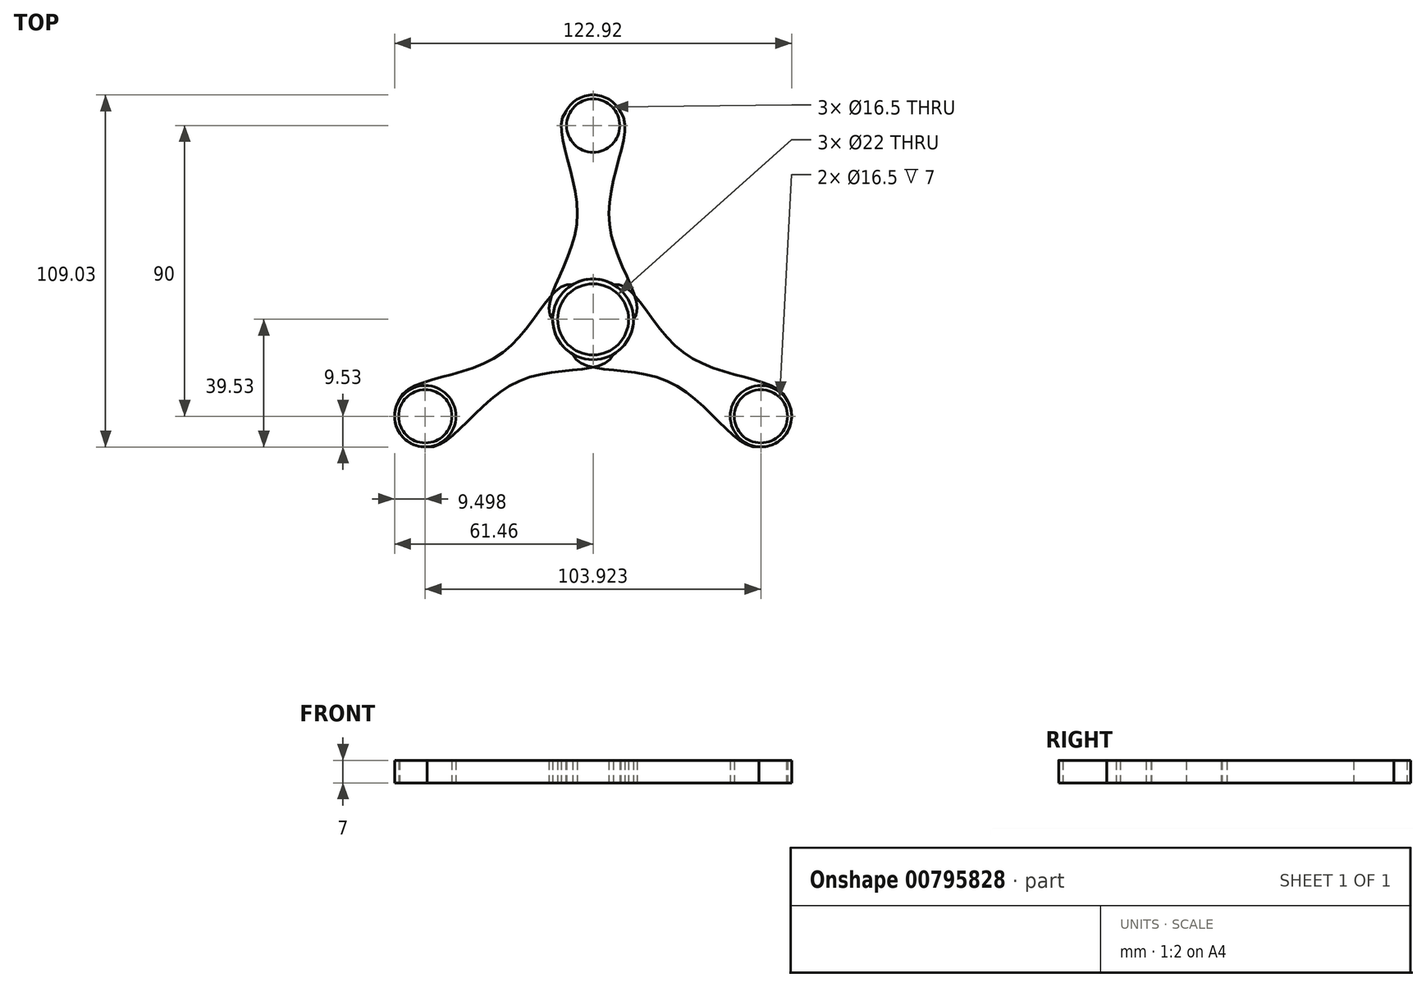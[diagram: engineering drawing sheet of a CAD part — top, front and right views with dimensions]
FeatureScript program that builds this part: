
annotation { "Feature Type Name" : "Feature", "Feature Type Description" : "" }
export const myFeature = defineFeature(function(context is Context, id is Id, definition is map)
    precondition{}
    {
        {
            var Q0;
            Q0=qCreatedBy(makeId("Top.planeOp"),FACE);
            var sketch = newSketch(context, id + "F0", { "sketchPlane" : qUnion([Q0])});
            skCircle(sketch, "E0", {"center": v(0, 0) * mm, "radius": 11 * mm});
            skLineSegment(sketch, "E1", {"start": v(0, 0) * mm, "end": v(0, 60) * mm});
            skLineSegment(sketch, "E2.1.0", {"start": v(0, 0) * mm, "end": v(-51.96, -30) * mm});
            skLineSegment(sketch, "E2.2.0", {"start": v(0, 0) * mm, "end": v(51.96, -30) * mm});
            skCircle(sketch, "E3", {"center": v(0, 60) * mm, "radius": 8.25 * mm});
            skCircle(sketch, "E4.1.0", {"center": v(-51.96, -30) * mm, "radius": 8.25 * mm});
            skCircle(sketch, "E4.2.0", {"center": v(51.96, -30) * mm, "radius": 8.25 * mm});
            skCircle(sketch, "E5", {"center": v(0, 60) * mm, "radius": 9.5 * mm});
            skCircle(sketch, "E6", {"center": v(0, 0) * mm, "radius": 12.5 * mm});
            skCircle(sketch, "E7.1.0", {"center": v(-51.96, -30) * mm, "radius": 9.5 * mm});
            skCircle(sketch, "E7.2.0", {"center": v(51.96, -30) * mm, "radius": 9.5 * mm});
            skPoint(sketch, "E8.1.internal.snap0", {"position": v(0, 30) * mm});
            skPoint(sketch, "E8.4.internal.snap0", {"position": v(0, 30) * mm});
            skFitSpline(sketch, "E8", {"points": [v(-8.52, 64.2) * mm, v(-5, 30) * mm, v(-12.5, 0) * mm, v(12.5, 0) * mm, v(5, 30) * mm, v(8.52, 64.2) * mm, v(-8.52, 64.2) * mm]});
            skSolve(sketch);
        }
        {
            var Q0;
            {var subQ0=sQuery(id+"F0.wireOp",EDGE,"E6");var subQ1=sQuery(id+"F0.wireOp",EDGE,"E1");var subQ2=makeQuery(id+"F0.imprint","INTERSECT",VERTEX,{"derivedFrom":[subQ1,subQ0]});Q0=makeQuery(id+"F0.imprint","IMPRINT",FACE,{"disambiguationData":[TD([[makeQuery(id+"F0.imprint","IMPRINT",EDGE,{"disambiguationData":[TD([[subQ2,-1.0]])],"derivedFrom":subQ1}),1.0]])]});}
            var Q1;
            {var subQ0=sQuery(id+"F0.wireOp",EDGE,"E6");var subQ1=sQuery(id+"F0.wireOp",EDGE,"E1");var subQ2=makeQuery(id+"F0.imprint","INTERSECT",VERTEX,{"derivedFrom":[subQ1,subQ0]});Q1=makeQuery(id+"F0.imprint","IMPRINT",FACE,{"disambiguationData":[TD([[makeQuery(id+"F0.imprint","IMPRINT",EDGE,{"disambiguationData":[TD([[subQ2,-1.0]])],"derivedFrom":subQ1}),-1.0]])]});}
            var Q2;
            {var subQ0=sQuery(id+"F0.wireOp",EDGE,"E8");var subQ1=sQuery(id+"F0.wireOp",EDGE,"E3");var subQ2=makeQuery(id+"F0.imprint","INTERSECT",VERTEX,{"disambiguationData":[OD(0.0)],"derivedFrom":[subQ1,subQ0]});Q2=makeQuery(id+"F0.imprint","IMPRINT",FACE,{"disambiguationData":[TD([[makeQuery(id+"F0.imprint","IMPRINT",EDGE,{"disambiguationData":[TD([[subQ2,1.0]])],"derivedFrom":subQ1}),-1.0]])]});}
            var Q3;
            {var subQ0=sQuery(id+"F0.wireOp",EDGE,"E3");var subQ1=sQuery(id+"F0.wireOp",EDGE,"E1");var subQ2=makeQuery(id+"F0.imprint","INTERSECT",VERTEX,{"derivedFrom":[subQ1,subQ0]});Q3=makeQuery(id+"F0.imprint","IMPRINT",FACE,{"disambiguationData":[TD([[makeQuery(id+"F0.imprint","IMPRINT",EDGE,{"disambiguationData":[TD([[subQ2,1.0]])],"derivedFrom":subQ1}),1.0]])]});}
            var Q4;
            {var subQ0=sQuery(id+"F0.wireOp",EDGE,"E3");var subQ1=sQuery(id+"F0.wireOp",EDGE,"E1");var subQ2=makeQuery(id+"F0.imprint","INTERSECT",VERTEX,{"derivedFrom":[subQ1,subQ0]});Q4=makeQuery(id+"F0.imprint","IMPRINT",FACE,{"disambiguationData":[TD([[makeQuery(id+"F0.imprint","IMPRINT",EDGE,{"disambiguationData":[TD([[subQ2,1.0]])],"derivedFrom":subQ1}),-1.0]])]});}
            var Q5;
            {var subQ0=sQuery(id+"F0.wireOp",EDGE,"E8");var subQ1=sQuery(id+"F0.wireOp",EDGE,"E0");var subQ2=makeQuery(id+"F0.imprint","INTERSECT",VERTEX,{"disambiguationData":[OD(0.0)],"derivedFrom":[subQ1,subQ0]});Q5=makeQuery(id+"F0.imprint","IMPRINT",FACE,{"disambiguationData":[TD([[makeQuery(id+"F0.imprint","IMPRINT",EDGE,{"disambiguationData":[TD([[subQ2,1.0]])],"derivedFrom":subQ1}),-1.0]])]});}
            var Q6;
            {var subQ0=sQuery(id+"F0.wireOp",EDGE,"E1");var subQ1=sQuery(id+"F0.wireOp",EDGE,"E0");var subQ2=makeQuery(id+"F0.imprint","INTERSECT",VERTEX,{"derivedFrom":[subQ1,subQ0]});Q6=makeQuery(id+"F0.imprint","IMPRINT",FACE,{"disambiguationData":[TD([[makeQuery(id+"F0.imprint","IMPRINT",EDGE,{"disambiguationData":[TD([[subQ2,1.0]])],"derivedFrom":subQ1}),-1.0]])]});}
            var Q7;
            {var subQ0=sQuery(id+"F0.wireOp",EDGE,"E8");var subQ1=sQuery(id+"F0.wireOp",EDGE,"E0");var subQ2=makeQuery(id+"F0.imprint","INTERSECT",VERTEX,{"disambiguationData":[OD(0.0)],"derivedFrom":[subQ1,subQ0]});Q7=makeQuery(id+"F0.imprint","IMPRINT",FACE,{"disambiguationData":[TD([[makeQuery(id+"F0.imprint","IMPRINT",EDGE,{"disambiguationData":[TD([[subQ2,-1.0]])],"derivedFrom":subQ1}),-1.0]])]});}
            var Q8;
            {var subQ0=sQuery(id+"F0.wireOp",EDGE,"E2.1.0");var subQ1=sQuery(id+"F0.wireOp",EDGE,"E0");var subQ2=makeQuery(id+"F0.imprint","INTERSECT",VERTEX,{"derivedFrom":[subQ1,subQ0]});Q8=makeQuery(id+"F0.imprint","IMPRINT",FACE,{"disambiguationData":[TD([[makeQuery(id+"F0.imprint","IMPRINT",EDGE,{"disambiguationData":[TD([[subQ2,-1.0]])],"derivedFrom":subQ1}),-1.0]])]});}
            var Q9;
            {var subQ0=sQuery(id+"F0.wireOp",EDGE,"E2.2.0");var subQ1=sQuery(id+"F0.wireOp",EDGE,"E0");var subQ2=makeQuery(id+"F0.imprint","INTERSECT",VERTEX,{"derivedFrom":[subQ1,subQ0]});Q9=makeQuery(id+"F0.imprint","IMPRINT",FACE,{"disambiguationData":[TD([[makeQuery(id+"F0.imprint","IMPRINT",EDGE,{"disambiguationData":[TD([[subQ2,-1.0]])],"derivedFrom":subQ1}),-1.0]])]});}
            var Q10;
            Q10=makeQuery(id+"F0.imprint","IMPRINT",FACE,{"disambiguationData":[TD([[makeQuery(id+"F0.imprint","IMPRINT",EDGE,{"derivedFrom":sQuery(id+"F0.wireOp",EDGE,"E7.2.0")}),1.0]])]});
            var Q11;
            Q11=makeQuery(id+"F0.imprint","IMPRINT",FACE,{"disambiguationData":[TD([[makeQuery(id+"F0.imprint","IMPRINT",EDGE,{"derivedFrom":sQuery(id+"F0.wireOp",EDGE,"E7.1.0")}),1.0]])]});
            extrude(context, id + "F1", {"entities" : qUnion([Q0, Q1, Q2, Q3, Q4, Q5, Q6, Q7, Q8, Q9, Q10, Q11]), "depth" : 7 * mm, "offsetDistance" : 25 * mm});
        }
        {
            var Q0;
            Q0=makeQuery(id+"F1.opExtrude","SWEPT_BODY",BODY,{"disambiguationData":[OSD([sQuery(id+"F0.wireOp",EDGE,"E5"),sQuery(id+"F0.wireOp",EDGE,"E6"),sQuery(id+"F0.wireOp",EDGE,"E8")])]});
            var Q1;
            Q1=makeQuery(id+"F1.opExtrude","SWEPT_FACE",FACE,{"disambiguationData":[OSD([sQuery(id+"F0.wireOp",EDGE,"E6")])]});
            circularPattern(context, id + "F2", {"entities" : qUnion([Q0]), "axis" : qUnion([Q1]), "angle" : 360 * degree, "instanceCount" : 3, "equalSpace" : true});
        }
    });
